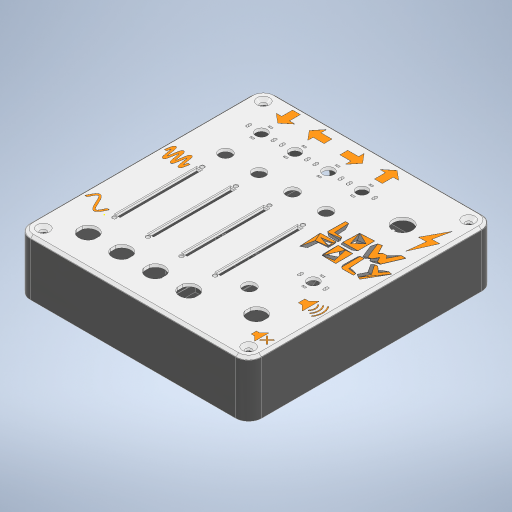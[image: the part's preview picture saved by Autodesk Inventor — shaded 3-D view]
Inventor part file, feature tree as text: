
AUTODESK INVENTOR PART (.ipt)
format: ipt  version: 2024.1 (Build 281209000, 209)  size: 8,071,680 bytes
history: native  units: mm
features: projected_geometry x59, sketch x58, extrude x57, fillet x24, other x13, chamfer x10, plane x2, pattern_linear x2
ambient origin geometry x8: Origin, YZ Plane, XZ Plane, XY Plane, X Axis, Y Axis, Z Axis, Center Point
bodies: Solid12 (feature_tree)
feature tree (225):
  other  "items"
  other  "Blocks"
  extrude  "Extrusion1"  Depth=9.5mm
  extrude  "Extrusion2"  Depth=9.5mm
  extrude  "Extrusion3"  Depth=12.0mm
  extrude  "Extrusion4"  Depth=12.0mm
  extrude  "Extrusion5"  Depth=3.3mm
  extrude  "Extrusion6"  Depth=4.0mm
  extrude  "Extrusion7"  Depth=3.3mm
  extrude  "Extrusion8"  Depth=3.3mm
  extrude  "Extrusion9"  Depth=3.3mm
  extrude  "Extrusion31"  Depth=4.3mm TaperAngle=0.0deg
  fillet  "Fillet1"  Radius=1.76mm
  extrude  "Extrusion10"  Depth=0.57mm
  plane  "Work Plane1"
  extrude  "Extrusion11"  Depth=4.96mm
  extrude  "Extrusion12"  Depth=1.22mm
  chamfer  "Chamfer1"  Distance=15.0mm
  extrude  "Extrusion13"  Depth=4.96mm
  fillet  "Fillet3"  Radius=0.49mm
  extrude  "Extrusion14"  Depth=5.0mm TaperAngle=0.0deg
  fillet  "Fillet4"  Radius=1.6mm
  extrude  "Extrusion15"  Depth=56.35mm
  extrude  "Extrusion16"  Depth=5.0mm TaperAngle=0.0deg
  extrude  "Extrusion17"  Depth=15.2mm
  extrude  "Extrusion21"  Depth=30.0mm
  extrude  "Extrusion30"  Depth=30.0mm
  fillet  "Fillet5"  Radius=10.35mm
  extrude  "Extrusion18"  Depth=1.2mm
  extrude  "Extrusion19"  Depth=7.5mm
  extrude  "Extrusion20"  Depth=5.9mm
  fillet  "Fillet6"  Radius=12.0mm
  extrude  "Extrusion22"  Depth=7.65mm
  extrude  "faceplate-extrude"  Depth=0.74mm
  fillet  "Fillet7"  Radius=9.2mm
  extrude  "Extrusion24"  Depth=4.0mm
  chamfer  "Chamfer2"  Distance=12.3mm
  chamfer  "Chamfer3"  Distance=2.0mm Angle=45.0deg
  sketch  "Sketch25"  dims[d64=0.5mm d65=7.65mm]
  extrude  "knob-extrude"  Depth=5.48mm TaperAngle=0.0deg
  extrude  "Extrusion26"  Depth=12.06mm
  extrude  "Extrusion27"  Depth=5.0mm
  chamfer  "Chamfer4"  Distance=12.3mm
  chamfer  "Chamfer5"  Distance=10.0mm
  extrude  "Extrusion28"  Depth=5.9mm
  fillet  "Fillet8"  Radius=10.0mm
  chamfer  "Chamfer6"  Distance=6.2mm
  fillet  "Fillet9"  Radius=16.0mm
  extrude  "Extrusion29"  Depth=14.5mm
  fillet  "Fillet10"  Radius=8.0mm
  chamfer  "Chamfer7"  Distance=28.0mm
  fillet  "Fillet11"  Radius=4.8mm
  chamfer  "Chamfer8"  Distance=17.15mm
  chamfer  "Chamfer9"  Distance=26.0mm
  extrude  "Extrusion32"  Depth=0.2mm
  extrude  "Extrusion33"  Depth=0.2mm
  fillet  "Fillet12"  Radius=2.87mm
  chamfer  "Chamfer10"  Distance=1.2mm
  extrude  "Extrusion34"  Depth=0.2mm
  extrude  "bracing"  Depth=0.2mm
  extrude  "Extrusion36"  Depth=0.2mm
  extrude  "graphics-controls"  Depth=0.2mm
  fillet  "Fillet13"  Radius=7.5mm
  fillet  "Fillet14"  Radius=7.5mm
  extrude  "waves"  Depth=0.2mm
  fillet  "Fillet15"  Radius=7.5mm
  fillet  "Fillet16"  Radius=7.5mm
  extrude  "logo"  Depth=0.2mm TaperAngle=0.0deg
  fillet  "Fillet17"  Radius=1.7mm
  extrude  "Extrusion41"  Depth=0.2mm
  extrude  "Extrusion42"  Depth=0.2mm
  extrude  "Extrusion43"  Depth=0.2mm TaperAngle=0.0deg
  extrude  "Extrusion44"  Depth=0.2mm
  fillet  "Fillet18"  Radius=0.2mm
  fillet  "Fillet19"  Radius=0.2mm
  fillet  "Fillet21"  Radius=0.8mm
  extrude  "Extrusion45"  Depth=0.2mm
  extrude  "Extrusion46"  Depth=0.2mm
  extrude  "Extrusion47"  Depth=0.2mm
  fillet  "Fillet20"  Radius=0.3mm
  extrude  "Extrusion48"  Depth=0.2mm
  fillet  "Fillet22"  Radius=0.1mm
  fillet  "Fillet23"  Radius=2.0mm
  plane  "Work Plane2"
  extrude  "Extrusion49"  Depth=0.2mm
  pattern_linear  "Rectangular Pattern1"  Spacing1=8.0mm  [1 undecoded]
  extrude  "Extrusion50"  Depth=0.2mm
  extrude  "Extrusion51"  TaperAngle=0.0deg  [1 undecoded]
  fillet  "Fillet24"  Radius=2.0mm
  extrude  "6.35-jack-hole"  Depth=0.2mm TaperAngle=45.0deg
  extrude  "Extrusion53"  Depth=0.2mm
  extrude  "Extrusion54"  Depth=0.2mm
  extrude  "Extrusion55"  Depth=0.2mm
  fillet  "Fillet25"  Radius=4.12mm
  extrude  "Extrusion56"  Depth=0.2mm
  extrude  "Extrusion57"  Depth=0.2mm
  extrude  "Extrusion58"  Depth=0.2mm TaperAngle=0.0deg
  pattern_linear  "Rectangular Pattern2"  Spacing1=6.5mm  [1 undecoded]
  sketch  "Sketch1"  dims[d0=60.0mm d1=9.5mm]
  sketch  "Sketch2"  dims[d2=9.5mm d3=9.5mm]
  sketch  "Sketch3"  dims[d4=9.5mm d5=12.0mm]
  sketch  "Sketch4"  dims[d6=12.0mm d7=12.0mm]
  projected_geometry  "Projected Loop1"
  sketch  "Sketch5"  dims[d8=6.0mm d9=0.0mm d10=3.3mm]
  projected_geometry  "Projected Loop2"
  projected_geometry  "Projected Loop3"
  projected_geometry  "Projected Loop4"
  sketch  "Sketch6"  dims[d11=3.3mm d12=4.0mm]
  sketch  "Sketch7"  dims[d13=4.0mm d14=3.3mm]
  sketch  "Sketch8"  dims[d15=3.3mm d16=3.3mm]
  sketch  "Sketch9"  dims[d17=3.3mm d18=3.3mm]
  projected_geometry  "Projected Loop5"
  sketch  "Sketch10"  dims[d19=3.3mm d20=4.3mm d21=0.0mm d22=1.76mm]
  projected_geometry  "Projected Loop6"
  sketch  "Sketch11"  dims[d24=2.9mm d25=0.57mm]
  projected_geometry  "Projected Loop7"
  sketch  "Sketch12"  dims[d26=1.97mm d27=4.96mm]
  sketch  "Sketch13"  dims[d28=1.495mm d29=1.22mm]
  sketch  "Sketch14"  dims[d30=0.27mm d31=15.0mm d32=0.0mm]
  sketch  "Sketch15"  dims[d33=3.98mm d34=4.96mm d35=0.49mm]
  sketch  "Sketch16"  dims[d36=5.0mm d37=0.0mm d38=5.0mm d39=0.0mm d40=1.6mm]
  sketch  "Sketch17"  dims[d41=1.825mm d42=56.35mm]
  projected_geometry  "Projected Loop8"
  sketch  "Sketch18"  dims[d43=1.825mm d44=5.0mm d45=0.0mm]
  sketch  "Sketch19"  dims[d46=19.0mm d47=15.2mm]
  projected_geometry  "Projected Loop9"
  sketch  "Sketch20"  dims[d48=16.4mm d49=30.0mm]
  projected_geometry  "Projected Loop10"
  sketch  "Sketch21"  dims[d50=30.0mm d51=30.0mm d53=10.35mm d54=0.0mm]
  projected_geometry  "Projected Loop11"
  projected_geometry  "Projected Loop12"
  projected_geometry  "Projected Loop13"
  projected_geometry  "Projected Loop14"
  projected_geometry  "Projected Loop15"
  projected_geometry  "Projected Loop16"
  projected_geometry  "Projected Loop17"
  projected_geometry  "Projected Loop18"
  projected_geometry  "Projected Loop19"
  projected_geometry  "Projected Loop20"
  projected_geometry  "Projected Loop21"
  sketch  "Sketch22"  dims[d55=6.8mm d56=1.2mm]
  projected_geometry  "Projected Loop22"
  projected_geometry  "Projected Loop23"
  projected_geometry  "Projected Loop24"
  projected_geometry  "Projected Loop25"
  projected_geometry  "Projected Loop26"
  sketch  "Sketch23"  dims[d57=2.87mm d58=7.5mm]
  other  "faceplate"
  sketch  "Sketch24"  dims[d59=4.5mm d60=0.0mm d61=5.9mm d62=12.0mm d63=0.0mm]
  sketch  "Sketch26"  dims[d67=13.0mm d68=0.74mm d69=9.2mm d70=0.0mm]
  projected_geometry  "Projected Loop27"
  other  "slider-knob"
  sketch  "Sketch27"  dims[d71=9.1mm d72=4.0mm d73=-1.745329mm]
  projected_geometry  "Projected Loop28"
  sketch  "Sketch28"  dims[d74=2.0mm]
  projected_geometry  "Projected Loop29"
  sketch  "Sketch29"  dims[d75=11.64mm]
  projected_geometry  "Projected Loop30"
  sketch  "Sketch30"  dims[d76=15.0mm]
  sketch  "Sketch31"  dims[d77=20.0mm d78=12.3mm d79=0.0mm d80=2.0mm d81=2.0mm d82=45.0deg]
  sketch  "Sketch32"  dims[d83=17.62mm d84=5.48mm d85=0.0mm]
  projected_geometry  "Projected Loop31"
  projected_geometry  "Projected Loop32"
  projected_geometry  "Projected Loop33"
  projected_geometry  "Projected Loop34"
  projected_geometry  "Projected Loop35"
  projected_geometry  "Projected Loop36"
  projected_geometry  "Projected Loop37"
  projected_geometry  "Projected Loop38"
  projected_geometry  "Projected Loop39"
  projected_geometry  "Projected Loop40"
  projected_geometry  "Projected Loop41"
  projected_geometry  "Projected Loop42"
  projected_geometry  "Projected Loop43"
  projected_geometry  "Projected Loop45"
  sketch  "Sketch33"  dims[d87=2.0mm d88=12.06mm]
  sketch  "Sketch34"  dims[d89=3.0mm d90=0.0mm d91=5.0mm]
  sketch  "Sketch35"  dims[d92=11.1mm]
  projected_geometry  "Projected Loop46"
  projected_geometry  "Projected Loop47"
  projected_geometry  "Projected Loop48"
  projected_geometry  "Projected Loop49"
  projected_geometry  "Projected Loop50"
  projected_geometry  "Projected Loop51"
  projected_geometry  "Projected Loop52"
  projected_geometry  "Projected Loop53"
  projected_geometry  "Projected Loop54"
  projected_geometry  "Projected Loop55"
  projected_geometry  "Projected Loop56"
  sketch  "Sketch36"  dims[d93=5.55mm]
  sketch  "Sketch37"  dims[d94=11.1mm]
  sketch  "Sketch38"  dims[d95=5.55mm]
  other  "2D Equation Curve1"
  sketch  "Sketch40"  dims[d96=11.1mm]
  other  "2D Equation Curve2"
  other  "2D Equation Curve4"
  other  "low-poly-logo"
  sketch  "Sketch42"  dims[d97=5.55mm]
  other  "000-low-poly-logo"
  sketch  "Sketch43"  dims[d98=11.1mm]
  projected_geometry  "Projected Loop57"
  other  "case-body"
  sketch  "Sketch44"  dims[d99=5.55mm]
  projected_geometry  "Projected Loop58"
  sketch  "Sketch45"  dims[d100=11.1mm]
  projected_geometry  "Projected Loop59"
  projected_geometry  "Projected Loop60"
  sketch  "Sketch46"  dims[d101=5.55mm]
  sketch  "Sketch47"  dims[d102=10.7mm]
  other  "circuit-boards"
  sketch  "Sketch48"  dims[d103=10.7mm]
  sketch  "Sketch49"  dims[d104=15.2mm]
  sketch  "Sketch50"  dims[d105=15.2mm]
  sketch  "Sketch51"  dims[d108=23.0mm]
  sketch  "Sketch52"  dims[d109=17.0mm d110=12.3mm d111=0.0mm]
  sketch  "Sketch53"  dims[d112=6.8mm]
  sketch  "Sketch54"  dims[d113=6.8mm d114=10.0mm d115=0.0mm]
  sketch  "Sketch55"  dims[d116=5.9mm d117=5.9mm d118=10.0mm d119=0.0mm]
  other  "jacks"
  sketch  "Sketch56"  dims[d120=0.2mm]
  sketch  "Sketch57"  dims[d121=11.9mm d122=6.2mm d123=0.0mm d124=16.0mm]
  sketch  "Sketch58"  dims[d125=29.0mm d126=14.5mm d127=8.0mm d128=28.0mm d129=0.0mm d130=4.8mm d131=17.15mm d132=0.523599mm]
  sketch  "Sketch59"  dims[d133=2.0mm]
  sketch  "Sketch60"  dims[d134=20.0mm d135=26.0mm d136=16.0mm d138=1.2mm d139=2.87mm d140=1.2mm d141=1.2mm d142=1.2mm d143=1.2mm d144=2.87mm d145=7.5mm d146=7.5mm d147=7.5mm d148=7.5mm d149=7.5mm d150=17.15mm d151=0.0mm d152=1.7mm d153=5.2mm d154=0.85mm d155=10.0mm d156=0.0mm d157=20.0mm d158=0.2mm d159=0.2mm d160=0.8mm d161=0.1mm d162=0.1mm d163=0.2mm d164=0.3mm d165=0.25mm d166=0.1mm d167=2.0mm d168=0.0mm d169=0.2mm d170=8.0mm d171=4.0mm d172=0.0mm d173=0.0mm d174=2.0mm d175=2.0mm d176=45.0deg d177=0.2mm d178=2.0mm d179=45.0deg d180=10.0mm d181=22.0mm d182=1.76mm d183=4.12mm d184=3.98mm d185=9.01mm d186=10.0mm d187=0.0mm d188=6.5mm d189=0.0mm d190=2.5mm d191=0.0mm d192=4.0mm d193=2.0mm d194=45.0deg d195=2.5mm d196=9.0mm d197=45.0deg d198=0.0mm d199=0.0mm d200=1.0mm d201=2.5mm d202=9.0mm d203=45.0deg d204=2.0mm d205=0.9mm d206=1.2mm d207=1.8mm d208=1.3mm d209=2.0mm d210=1.5mm d211=1.0mm d212=0.0mm d213=0.0mm d214=0.4mm d215=3.341737mm d216=2.5mm d217=9.0mm d218=45.0deg d219=0.5mm d221=7.5mm d222=7.5mm d223=7.5mm d224=7.5mm d225=1.2mm d226=1.2mm d227=1.2mm d228=1.2mm d229=5.5mm d230=1.9mm d231=0.77mm d232=1.9mm d233=0.77mm d234=1.9mm d235=0.77mm d236=1.9mm d237=0.77mm d238=1.9mm d239=0.77mm d240=1.9mm d241=0.77mm d242=1.9mm d243=0.77mm d244=1.9mm d245=0.77mm d246=5.5mm d247=1.4mm d248=0.0mm d249=1.2mm d253=1.2mm d255=7.5mm d256=2.87mm d257=1.9mm d258=0.77mm d259=1.9mm d260=0.77mm d261=11.0mm d262=5.5mm d263=1.4mm d264=0.0mm d265=0.2mm d266=0.5mm d267=2.0mm d268=45.0deg d269=1.5mm d270=2.0mm d271=45.0deg d273=1.5mm d274=0.5mm d275=0.0mm d276=25.0mm d277=0.4mm d278=0.0mm d279=2.0mm d280=0.4mm d281=2.0mm d282=45.0deg d283=12.0mm d284=1.5mm d285=0.0mm d286=1.5mm d287=0.0mm d288=21.0mm d289=1.5mm d290=0.0mm d304=7.0mm d314=5.0mm d315=5.0mm d316=12.0mm d317=2.0mm d318=12.0mm d319=7.0mm d320=7.0mm d321=5.0mm d322=5.0mm d323=5.0mm d324=5.0mm d325=7.0mm d326=5.0mm d327=5.0mm d328=12.0mm d329=12.0mm d330=3.0mm d331=4.2mm d332=3.36mm d333=2.52mm d334=3.36mm d335=10.92mm d336=0.672mm d337=2.94mm d338=2.94mm d339=4.116mm d340=4.116mm d341=5.208mm d342=0.672mm d343=0.672mm d344=1.68mm d345=1.68mm d346=1.68mm d347=3.36mm d348=2.94mm d349=2.1mm d350=2.94mm d351=13.0mm d363=45.0deg d364=90.0deg d365=3.36mm d366=0.756mm d367=0.756mm d368=2.1mm d369=2.1mm d370=0.0mm d371=10.0mm d372=0.05mm d373=0.0mm d374=0.1mm d375=0.05mm d376=0.0mm d377=10.0mm d380=0.0mm d381=3600.0mm d390=0.0mm d391=10800.0mm d394=0.0mm d395=10800.0mm d396=1.5mm d397=1.0mm d398=3.0mm d400=0.0mm d401=3600.0mm d402=1.5mm d403=3.0mm d404=1.0mm d405=0.05mm d406=0.0mm d407=1.0mm d408=0.15mm d422=5.208mm d426=0.05mm d427=0.0mm d428=60.0mm d429=32.0mm d430=0.1mm d431=0.1mm d432=0.1mm d435=0.1mm d437=30.0mm d438=0.0mm d439=0.4mm d440=2.0mm d441=2.0mm d442=0.0mm d443=2.0mm d444=0.0mm d445=43.0mm d446=55.0mm d447=3.0mm d448=3.0mm d449=6.0mm d450=0.0mm d451=2.0mm d452=5.0mm d453=43.0mm d454=55.0mm d455=3.0mm d456=3.0mm d457=3.0mm d458=4.0mm d459=0.0mm d460=10.1mm d461=19.1mm d462=11.2mm d463=23.0mm d464=7.0mm d465=0.0mm d466=16.4mm d469=32.0mm d470=0.0mm d471=1.0mm d473=4.12mm d474=5.5mm d475=1.0mm d476=0.5mm d477=3.2mm d478=5.0mm d479=3.0mm d481=5.0mm d482=5.0mm d483=5.0mm d484=3.0mm d485=4.0mm d486=4.0mm d487=5.0mm d488=8.0mm d489=44.0mm d490=0.0mm d491=0.0mm d492=260.0mm d493=3.0mm d494=30.0mm d495=11.5mm d496=11.5mm d497=3.0mm d498=0.0mm d499=30.0mm d501=11.0mm d502=5.0mm d503=4.0mm d504=6.0mm d505=0.0mm d506=4.999995mm d507=5.0mm d508=1.5mm d509=1.499992mm d510=3.0mm d511=1.5mm d512=5.0mm d513=6.0mm d514=28.0mm d515=0.0mm d516=0.0mm d517=200.0mm d518=11.0mm d519=20.0mm d520=8.0mm d521=22.0mm d522=6.0mm d523=0.0mm d524=10.83mm d525=8.5mm d526=0.0mm d527=6.5mm d528=20.1mm d529=10.05mm d530=7.9mm d531=14.8mm d532=26.0mm d533=0.0mm d534=0.4mm d535=0.4mm d536=1.3mm d537=1.3mm d538=1.3mm d539=3.4mm d540=2.0mm d541=2.0mm d542=5.05mm d543=5.05mm d544=4.5mm d545=0.0mm d546=0.6mm d547=24.0mm d548=14.0mm d549=11.5mm d550=0.0mm d551=0.0mm d552=18.0mm d553=22.0mm d554=0.0mm d555=4.0mm d556=3.0mm d557=22.0mm d558=0.0mm d559=20.0mm d561=131.6mm d562=20.0mm d564=141.0mm]
  other  "000-low-poly-logo:1"
note: 3 required parameter values undecoded (feature->parameter linkage not recoverable at this tier; creation-order binding heuristic only, values carry confidence <= 0.55)
